FCSTD DOCUMENT  (FreeCAD 1.0R39319 (Git))
Label: week2 sketch 2
License: All rights reserved
LicenseURL: https://en.wikipedia.org/wiki/All_rights_reserved
objects: Sketcher::SketchObject×1, PartDesign::Body×1
note: 3 computed .brp shape members not serialized (recipe doc carries the construction recipe); baked Part::Feature solids carry a one-line shape summary decoded from their .brp

FEATURE [Sketcher::SketchObject] Sketch
  ArcFitTolerance = 1e-06
  AttachmentSupport = -> [XY_Plane]
  FullyConstrained = true
  MakeInternals = false
  MapMode = 5
  sketch-geometry (34):
    g0: ArcOfCircle CenterX=0 CenterY=0 CenterZ=0 NormalX=0 NormalY=0 NormalZ=1 AngleXU=0 Radius=30 StartAngle=4.71239 EndAngle=7.85398
    g1: ArcOfCircle CenterX=-70 CenterY=4.104e-13 CenterZ=0 NormalX=0 NormalY=0 NormalZ=1 AngleXU=0 Radius=30 StartAngle=1.5708 EndAngle=4.71239
    g2: LineSegment StartX=-5.5e-15 StartY=-30 StartZ=0 EndX=-16 EndY=-30 EndZ=0
    g3: LineSegment StartX=9.2e-15 StartY=30 StartZ=0 EndX=-70 EndY=30 EndZ=0
    g4: ArcOfCircle CenterX=0 CenterY=-2.016e-13 CenterZ=0 NormalX=0 NormalY=0 NormalZ=1 AngleXU=0 Radius=45 StartAngle=4.71239 EndAngle=7.85398
    g5: ArcOfCircle CenterX=-70 CenterY=4.104e-13 CenterZ=0 NormalX=0 NormalY=0 NormalZ=1 AngleXU=0 Radius=45 StartAngle=1.5708 EndAngle=4.71239
    g6: LineSegment StartX=5.5e-15 StartY=-45 StartZ=0 EndX=-16 EndY=-45 EndZ=0
    g7: LineSegment StartX=0 StartY=45 StartZ=0 EndX=-70 EndY=45 EndZ=0
    g8: LineSegment StartX=-61 StartY=30 StartZ=0 EndX=-61 EndY=45 EndZ=0
    g9: LineSegment StartX=-9 StartY=30 StartZ=0 EndX=-9 EndY=45 EndZ=0
    g10: ArcOfCircle CenterX=-53 CenterY=45 CenterZ=0 NormalX=0 NormalY=0 NormalZ=1 AngleXU=0 Radius=8 StartAngle=1.5708 EndAngle=3.14159
    g11: ArcOfCircle CenterX=-17 CenterY=45 CenterZ=0 NormalX=0 NormalY=0 NormalZ=1 AngleXU=0 Radius=8 StartAngle=0 EndAngle=1.5708
    g12: LineSegment StartX=-53 StartY=53 StartZ=0 EndX=-17 EndY=53 EndZ=0
    g13: LineSegment StartX=-16 StartY=-30 StartZ=0 EndX=-16 EndY=-77.5 EndZ=0
    g14: LineSegment StartX=-54 StartY=-30 StartZ=0 EndX=-54 EndY=-77.5 EndZ=0
    g15: Circle CenterX=7 CenterY=-77.5 CenterZ=0 NormalX=0 NormalY=0 NormalZ=1 AngleXU=0 Radius=23
    g16: Circle CenterX=7 CenterY=-77.5 CenterZ=0 NormalX=0 NormalY=0 NormalZ=1 AngleXU=0 Radius=12.5
    g17: ArcOfCircle CenterX=24.248 CenterY=-49.3663 CenterZ=0 NormalX=0 NormalY=0 NormalZ=1 AngleXU=0 Radius=10 StartAngle=2.02737 EndAngle=4.16241
    g18: LineSegment [constr] StartX=-35 StartY=125.044 StartZ=0 EndX=-35 EndY=-158.492 EndZ=0
    g19: ArcOfCircle CenterX=-94.2481 CenterY=-49.3663 CenterZ=0 NormalX=0 NormalY=0 NormalZ=1 AngleXU=0 Radius=10 StartAngle=5.26237 EndAngle=7.39741
    g20: Circle CenterX=-77 CenterY=-77.5 CenterZ=0 NormalX=0 NormalY=0 NormalZ=1 AngleXU=0 Radius=23
    g21: Circle CenterX=-77 CenterY=-77.5 CenterZ=0 NormalX=0 NormalY=0 NormalZ=1 AngleXU=0 Radius=12.5
    g22: LineSegment StartX=-54 StartY=-30 StartZ=0 EndX=-70 EndY=-30 EndZ=0
    g23: LineSegment StartX=-54 StartY=-45 StartZ=0 EndX=-70 EndY=-45 EndZ=0
    g24: ArcOfCircle CenterX=-22 CenterY=68 CenterZ=0 NormalX=0 NormalY=0 NormalZ=1 AngleXU=0 Radius=10 StartAngle=4.71239 EndAngle=7.85398
    g25: ArcOfCircle CenterX=-48 CenterY=68 CenterZ=0 NormalX=0 NormalY=0 NormalZ=1 AngleXU=0 Radius=10 StartAngle=1.5708 EndAngle=4.71239
    g26: LineSegment StartX=-22 StartY=58 StartZ=0 EndX=-48 EndY=58 EndZ=0
    g27: LineSegment StartX=-22 StartY=78 StartZ=0 EndX=-48 EndY=78 EndZ=0
    g28: ArcOfCircle CenterX=-22 CenterY=68 CenterZ=0 NormalX=0 NormalY=0 NormalZ=1 AngleXU=0 Radius=15 StartAngle=4.71239 EndAngle=7.85398
    g29: ArcOfCircle CenterX=-48 CenterY=68 CenterZ=0 NormalX=0 NormalY=0 NormalZ=1 AngleXU=0 Radius=15 StartAngle=1.5708 EndAngle=4.71239
    g30: LineSegment StartX=-22 StartY=53 StartZ=0 EndX=-48 EndY=53 EndZ=0
    g31: LineSegment StartX=-22 StartY=83 StartZ=0 EndX=-48 EndY=83 EndZ=0
    g32: ArcOfCircle CenterX=-25.1308 CenterY=-3.42828 CenterZ=0 NormalX=0 NormalY=0 NormalZ=1 AngleXU=0 Radius=90 StartAngle=1.88065 EndAngle=3.06533
    g33: ArcOfCircle CenterX=-44.8692 CenterY=-3.42828 CenterZ=0 NormalX=0 NormalY=0 NormalZ=1 AngleXU=0 Radius=90 StartAngle=0.0762578 EndAngle=1.26094
  constraints (90):
    c: Tangent(g0,g2) = 1.5708
    c: Tangent(g0,g3) = -1.5708
    c: Coincident(g1,g22)
    c: Tangent(g1,g3) = -1.5708
    c: Equal(g0,g1)
    c: Horizontal(g3)
    c: Coincident(g0,g-1)
    c: Tangent(g4,g6) = 1.5708
    c: Tangent(g4,g7) = -1.5708
    c: Coincident(g5,g23)
    c: Tangent(g5,g7) = -1.5708
    c: Equal(g4,g5)
    c: Horizontal(g7)
    c: Coincident(g5,g1)
    c: PointOnObject(g4,g-2)
    c: Distance(g6,g2) = 15
    c: Radius(g1) = 30
    c: PointOnObject(g8,g3)
    c: Vertical(g8)
    c: PointOnObject(g9,g3)
    c: Vertical(g9)
    c: Distance(g-2,g9) = 9
    c: Distance(g1,g8) = 9
    c: PointOnObject(g8,g7)
    c: PointOnObject(g9,g7)
    c: PointOnObject(g10,g7)
    c: Coincident(g10,g8)
    c: PointOnObject(g11,g7)
    c: Coincident(g11,g9)
    c: Equal(g10,g11)
    c: Coincident(g12,g10)
    c: Tangent(g12,g11) = 1.5708
    c: Horizontal(g12)
    c: Radius(g10) = 8
    c: Vertical(g13)
    c: PointOnObject(g14,g22)
    c: Vertical(g14)
    c: Distance(g4,g13) = 16
    c: Distance(g5,g14) = 16
    c: Distance(g14,g13) = 38
    c: Coincident(g16,g15)
    c: Diameter(g15) = 46
    c: Diameter(g16) = 25
    c: Radius(g17) = 10
    c: Tangent(g13,g15) = -1.5708
    c: Tangent(g17,g4) = 1.5708
    c: Tangent(g17,g15) = 1.5708
    c: Distance(g15,g-1) = 77.5
    c: Symmetric(g10,g11,g18)
    c: Block(g18)
    c: Coincident(g21,g20)
    c: Diameter(g20) = 46
    c: Diameter(g21) = 25
    c: Radius(g19) = 10
    c: Tangent(g19,g20) = 1.5708
    c: Tangent(g19,g5) = 1.5708
    c: Distance(g20,g-1) = 77.5
    c: Tangent(g14,g20) = 1.5708
    c: PointOnObject(g22,g14)
    c: Coincident(g2,g13)
    c: PointOnObject(g23,g14)
    c: PointOnObject(g6,g13)
    c: Horizontal(g2)
    c: Horizontal(g6)
    c: Horizontal(g22)
    c: Horizontal(g23)
    c: Equal(g23,g22)
    c: Tangent(g24,g26) = 1.5708
    c: Tangent(g24,g27) = -1.5708
    c: Tangent(g25,g26) = 1.5708
    c: Tangent(g25,g27) = -1.5708
    c: Equal(g24,g25)
    c: Symmetric(g25,g24,g18)
    c: Tangent(g28,g30) = 1.5708
    c: Tangent(g28,g31) = -1.5708
    c: Tangent(g29,g30) = 1.5708
    c: Tangent(g29,g31) = -1.5708
    c: Equal(g28,g29)
    c: Coincident(g28,g24)
    c: Coincident(g29,g25)
    c: Distance(g27,g31) = 5
    c: Radius(g25) = 10
    c: DistanceX(g25,g24) = 26
    c: PointOnObject(g29,g12)
    c: Tangent(g32,g5) = -1.5708
    c: Tangent(g32,g29) = -1.5708
    c: Radius(g32) = 90
    c: Radius(g33) = 90
    c: Tangent(g33,g28) = -1.5708
    c: Tangent(g33,g4) = -1.5708
FEATURE [PartDesign::Body] Body
  AllowCompound = false
  Group = -> [Sketch]
  Origin = -> Origin
